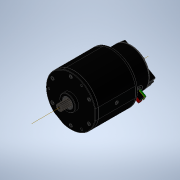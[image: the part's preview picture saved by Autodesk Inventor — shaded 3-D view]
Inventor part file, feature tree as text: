
AUTODESK INVENTOR PART (.ipt)
format: ipt  version: 2020 (Build 240168000, 168)  size: 13,614,080 bytes
history: native  units: in
note: dims shown in document units (in); Inventor stores cm internally (conversion verified against a paired STEP export)
features: other x46, sketch x2, extrude x1, hole x1
ambient origin geometry x8: Origin, YZ Plane, XZ Plane, XY Plane, X Axis, Y Axis, Z Axis, Center Point
bodies: Solid1 (feature_tree), Solid2 (feature_tree), Solid3 (feature_tree), Solid4 (feature_tree), Solid5 (feature_tree), Solid6 (feature_tree), Solid7 (feature_tree), Solid8 (feature_tree), Solid9 (feature_tree), Solid10 (feature_tree), Solid11 (feature_tree), Solid12 (feature_tree), Solid13 (feature_tree), Solid14 (feature_tree), Solid15 (feature_tree), Solid16 (feature_tree), Solid17 (feature_tree), Solid18 (feature_tree), Solid19 (feature_tree), Solid20 (feature_tree), Solid21 (feature_tree), Solid22 (feature_tree), Solid23 (feature_tree), Solid24 (feature_tree), Solid25 (feature_tree), Solid26 (feature_tree), Solid27 (feature_tree), Solid28 (feature_tree), Solid29 (feature_tree), Solid30 (feature_tree), Solid31 (feature_tree), Solid32 (feature_tree), Solid33 (feature_tree), Solid34 (feature_tree), Solid35 (feature_tree), Solid36 (feature_tree), Solid37 (feature_tree), Solid38 (feature_tree), Solid39 (feature_tree), Solid40 (feature_tree), Solid41 (feature_tree), Solid42 (feature_tree), Solid43 (feature_tree)
feature tree (50):
  other  "217-6515-201 Rev6_28:1"
  other  "Work Axis1"
  extrude  "Extrusion1"  [1 undecoded]
  hole  "Hole1"  [1 undecoded]
  sketch  "Sketch1"  dims[d0=0.8228in d1=0.0in]
  sketch  "Sketch2"  dims[d2=0.13in d3=0.328in d4=0.1575in d5=0.0787in d6=90.0deg d7=0.4843in d8=0.8108in]
  other  "217-6515-Back 20190920_1:1"
  other  "217-6515-202 Rev6_29:1"
  other  "217-6515-002 Rev6_3:1"
  other  "M2.5 SHCS, Grade 8 Steel Rev1_SSAM2.5-06MMZB_4:1"
  other  "M2.5 SHCS, Grade 8 Steel Rev1_SSAM2.5-06MMZB_5:1"
  other  "M2.5 SHCS, Grade 8 Steel Rev1_SSAM2.5-06MMZB_6:1"
  other  "M2.5 SHCS, Grade 8 Steel Rev1_SSAM2.5-06MMZB_7:1"
  other  "M2.5 SHCS, Grade 8 Steel Rev1_SSAM2.5-06MMZB_8:1"
  other  "217-6515-010 Rev1_9262K442_9:1"
  other  "217-6515-001 Rev6_10:1"
  other  "217-6515-005 Rev4_7804K116_11:1"
  other  "217-6515-005 Rev4_7804K116_11:2"
  other  "217-6515-005 Rev4_7804K116_11:3"
  other  "217-6515-005 Rev4_7804K116_11:4"
  other  "217-6515-005 Rev4_7804K116_11:5"
  other  "217-6515-005 Rev4_7804K116_11:6"
  other  "217-6515-005 Rev4_7804K116_11:7"
  other  "217-6515-005 Rev4_7804K116_11:8"
  other  "217-6515-005 Rev4_7804K116_11:9"
  other  "217-6515-005 Rev4_7804K116_11:10"
  other  "217-6515-005 Rev4_7804K116_11:11"
  other  "217-6515-005 Rev4_7804K116_11:12"
  other  "217-6515-005 Rev4_7804K116_11:13"
  other  "217-6515-005 Rev4_7804K116_11:14"
  other  "217-6515-005 Rev4_7804K116_11:15"
  other  "217-6515-005 Rev4_7804K116_11:16"
  other  "M3 BHTS-SECURE, Grade 8 Steel Rev1_SBTM3-24MMZB-SECURE_12:1"
  other  "M3 BHTS-SECURE, Grade 8 Steel Rev1_SBTM3-24MMZB-SECURE_13:1"
  other  "M3 BHTS-SECURE, Grade 8 Steel Rev1_SBTM3-24MMZB-SECURE_14:1"
  other  "M3 BHTS, Grade 8 Steel Rev1_SBTM3-50MMZB_15:1"
  other  "M3 BHTS, Grade 8 Steel Rev1_SBTM3-50MMZB_16:1"
  other  "M3 BHTS, Grade 8 Steel Rev1_SBTM3-50MMZB_17:1"
  other  "217-6515-308 Rev5_18:1"
  other  "#4-40 SHCS, Grade 8 Steel Rev2_SSA0440-0125ZB_19:1"
  other  "#4-40 SHCS, Grade 8 Steel Rev2_SSA0440-0125ZB_20:1"
  other  "217-4649-007 Rev1_94105A824_21:1"
  other  "217-4649-007 Rev1_94105A824_22:1"
  other  "217-4649-007 Rev1_94105A824_23:1"
  other  "217-4649-007 Rev1_94105A824_24:1"
  other  "217-4649-007 Rev1_94105A824_25:1"
  other  "217-4649-007 Rev1_94105A824_26:1"
  other  "217-4649-007 Rev1_94105A824_27:1"
  other  "Composite1"
  other  "Srf1"
note: 2 required parameter values undecoded (feature->parameter linkage not recoverable at this tier; creation-order binding heuristic only, values carry confidence <= 0.55)
